# Revit family: Zumtobel INTRO
name_source: partatom
category: Lighting Fixtures
revit_build: Autodesk Revit 2014 (Build: 20140709_2115(x64)
units: mm (PartAtom-declared; Revit-internal decimal feet)

## types (2) — shared parameters
Assembly Code = D5020200
Body = Zumtobel_Metal_White
Cover = Zumtobel_Lamp_Self_llumination_Opaque
Description = LED spotlight
Height = 142 mm  [stored 0.465879 ft]
Lamp = LED
Manufacturer = Zumtobel Lighting
URL = http://www.zumtobel.com
Voltage = 230 V
zero-valued in all types: Default Elevation

## per-type parameters (varying)
| type | Apparent Load | Body Offset | Body R M R1 | Body R1 | Body Type | Cut Out Diameter | Length | Model | Width |
| INTRO-R M R1 | 36 VA | -54.62 mm  [stored -0.179199 ft] | Yes | No | Zumtobel INTRO Body : INTRO-R M R1 | 189 mm  [stored 0.620079 ft] | 206 mm  [stored 0.675853 ft] | 60815671 | 206 mm  [stored 0.675853 ft] |
| INTRO R1 | 29 VA | -56.62 mm  [stored -0.185761 ft] | No | Yes | Zumtobel INTRO Body : INTRO-R1 | 180 mm  [stored 0.590551 ft] | 203 mm  [stored 0.66601 ft] | 60814504 | 203 mm  [stored 0.66601 ft] |

note: [stored X ft] marks values corroborated as IEEE doubles in the binary element streams (Revit-internal decimal feet)

## geometry (parser evidence)
native form markers: Sweep x5
no freeform markers — native parametric forms only
